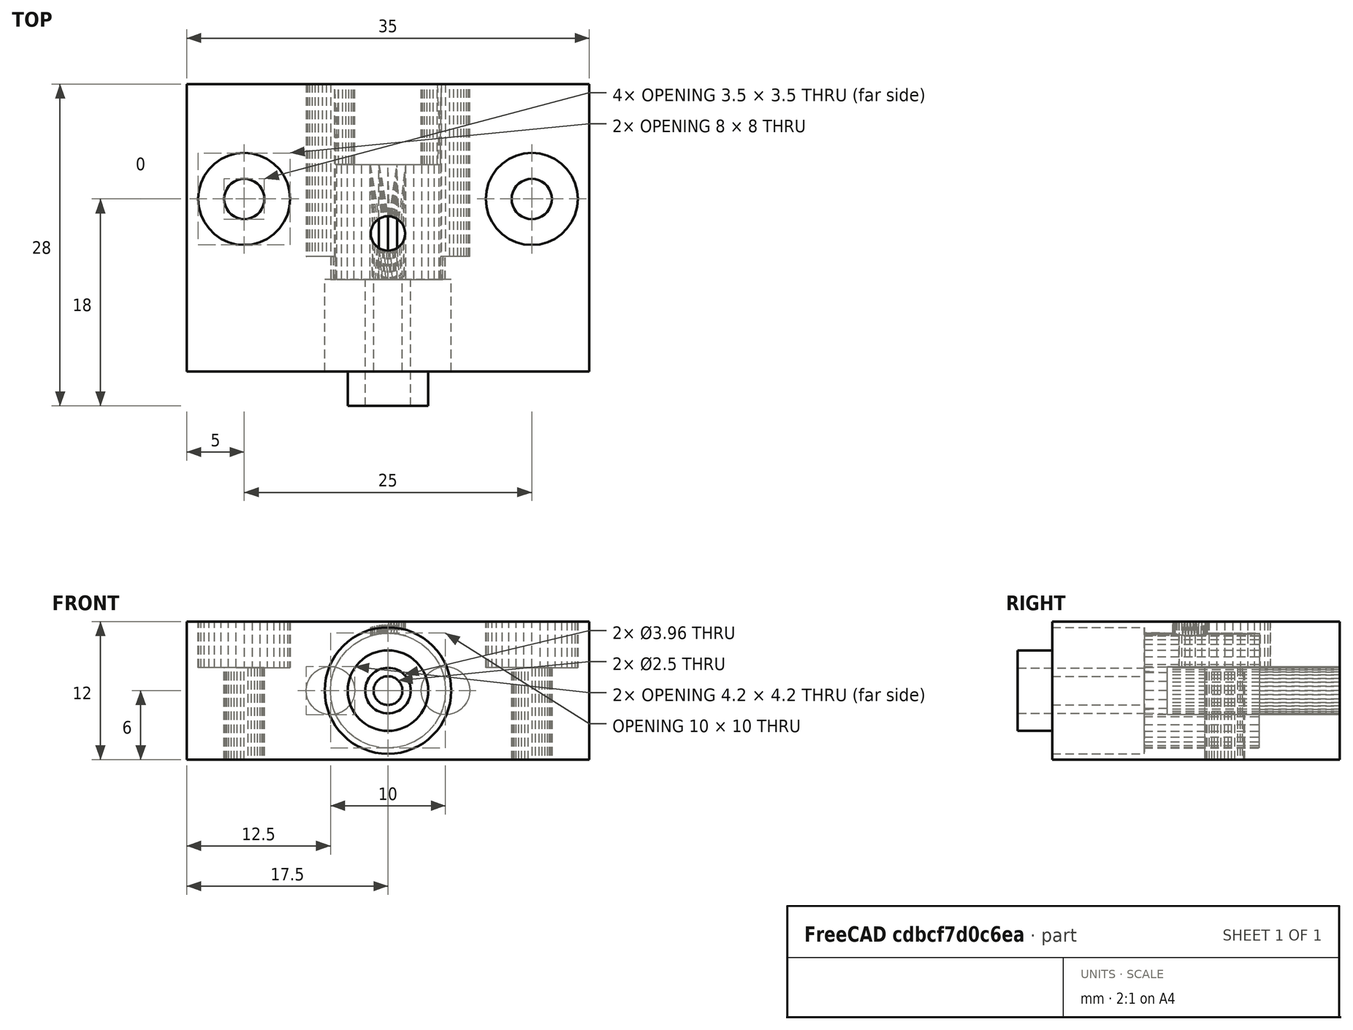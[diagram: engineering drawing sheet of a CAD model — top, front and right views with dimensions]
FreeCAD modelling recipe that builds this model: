
FCSTD DOCUMENT  (FreeCAD 0.18R14715 (Git))
Label: large_manipulator_manifold_modifications
License: All rights reserved
LicenseURL: http://en.wikipedia.org/wiki/All_rights_reserved
objects: Part::Feature×5, Part::Cylinder×5, Part::MultiFuse×3, Part::Cut×2
note: 15 computed .brp shape members not serialized (recipe doc carries the construction recipe); baked Part::Feature solids carry a one-line shape summary decoded from their .brp

FEATURE [Part::Feature] LargeManipulatorManifold001001  label="refined_lmm_import"
  shape: bbox 35 x 25 x 12 mm, 445 faces, 0 solids (baked)
FEATURE [Part::Cylinder] Cylinder  label="10-32_support"
  Angle = 360
  AttacherType = Attacher::AttachEngine3D
  Height = 8
  Placement = pos=(17.5,0,6) rot=(-1,0,0;1.5708rad)
  Radius = 5.5
  expr: Placement.Rotation.Angle = 270
FEATURE [Part::Cylinder] Cylinder001  label="10-32_tap_hole"
  Angle = 360
  AttacherType = Attacher::AttachEngine3D
  Height = 11
  Placement = pos=(17.5,-3,6) rot=(-1,0,0;1.5708rad)
  Radius = 1.98
  expr: Height = 8mm + thin_neck.Height
  expr: Placement.Base.y = -thin_neck.Height
FEATURE [Part::Feature] LargeManipulatorManifold001001_solid  label="refined_lmm_import (Solid)"
  shape: bbox 35 x 25 x 12 mm, 445 faces (baked)
FEATURE [Part::Cylinder] Cylinder002  label="M3_support"
  Angle = 360
  AttacherType = Attacher::AttachEngine3D
  Height = 8
  Placement = pos=(17.5,0,6) rot=(-1,0,0;1.5708rad)
  Radius = 5.5
  expr: Placement.Rotation.Angle = 270
FEATURE [Part::Cylinder] Cylinder003  label="M3_tap_hole"
  Angle = 360
  AttacherType = Attacher::AttachEngine3D
  Height = 8
  Placement = pos=(17.5,0,6) rot=(-1,0,0;1.5708rad)
  Radius = 1.25
FEATURE [Part::Cut] Cut001  label="M3_support_and_tap_hole"
  Base = -> Cylinder002
  Tool = -> Cylinder003
FEATURE [Part::Feature] LargeManipulatorManifold001001_solid001  label="refined_lmm_import (Solid) 2"
  shape: bbox 35 x 25 x 12 mm, 445 faces (baked)
FEATURE [Part::Feature] Cut001_solid  label="M3_support_and_tap_hole (Solid)"
  shape: bbox 11 x 8 x 11 mm, 4 faces (baked)
FEATURE [Part::MultiFuse] Fusion001  label="M3_large_manipulator_manifold"
  Shapes = -> [LargeManipulatorManifold001001_solid001,Cut001_solid]
FEATURE [Part::Cylinder] Cylinder004  label="thin_neck"
  Angle = 360
  AttacherType = Attacher::AttachEngine3D
  Height = 3
  Placement = pos=(17.5,0,6) rot=(-1,0,0;4.71239rad)
  Radius = 3.5
  expr: Placement.Rotation.Angle = 270
FEATURE [Part::MultiFuse] Fusion002  label="10-32_support_with_neck"
  Shapes = -> [Cylinder,Cylinder004]
FEATURE [Part::Cut] Cut  label="10-32_support_neck_and_taphole"
  Base = -> Fusion002
  Tool = -> Cylinder001
FEATURE [Part::Feature] Cut_solid001  label="10-32_support_neck_and_taphole (Solid)"
  shape: bbox 11 x 11 x 11 mm, 6 faces (baked)
FEATURE [Part::MultiFuse] Fusion  label="10-32_large_manipulator_manifold_with_neck"
  Shapes = -> [LargeManipulatorManifold001001_solid,Cut_solid001]
